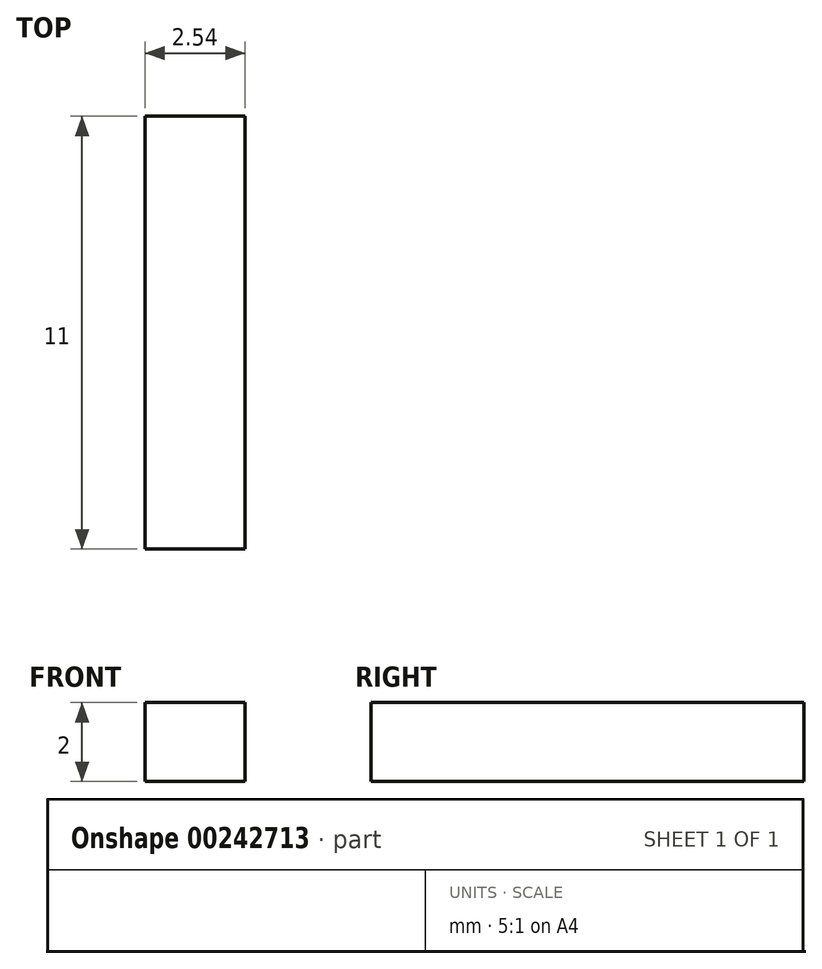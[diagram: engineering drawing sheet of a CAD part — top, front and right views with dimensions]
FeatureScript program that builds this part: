
annotation { "Feature Type Name" : "Feature", "Feature Type Description" : "" }
export const myFeature = defineFeature(function(context is Context, id is Id, definition is map)
    precondition{}
    {
        {
            var Q0;
            Q0=qCreatedBy(makeId("Front.planeOp"),FACE);
            var sketch = newSketch(context, id + "F0", { "sketchPlane" : qUnion([Q0])});
            skLineSegment(sketch, "E0.bottom", {"start": v(1.27, 1) * mm, "end": v(-1.27, 1) * mm});
            skLineSegment(sketch, "E0.top", {"start": v(1.27, -1) * mm, "end": v(-1.27, -1) * mm});
            skLineSegment(sketch, "E0.left", {"start": v(1.27, 1) * mm, "end": v(1.27, -1) * mm});
            skLineSegment(sketch, "E0.right", {"start": v(-1.27, 1) * mm, "end": v(-1.27, -1) * mm});
            skPoint(sketch, "E0.middle", {"position": v(0, 0) * mm});
            skSolve(sketch);
        }
        {
            var Q0;
            Q0 = qSketchRegion(id + "F0", true);
            extrude(context, id + "F1", {"entities" : qUnion([Q0]), "depth" : 11 * mm});
        }
    });
